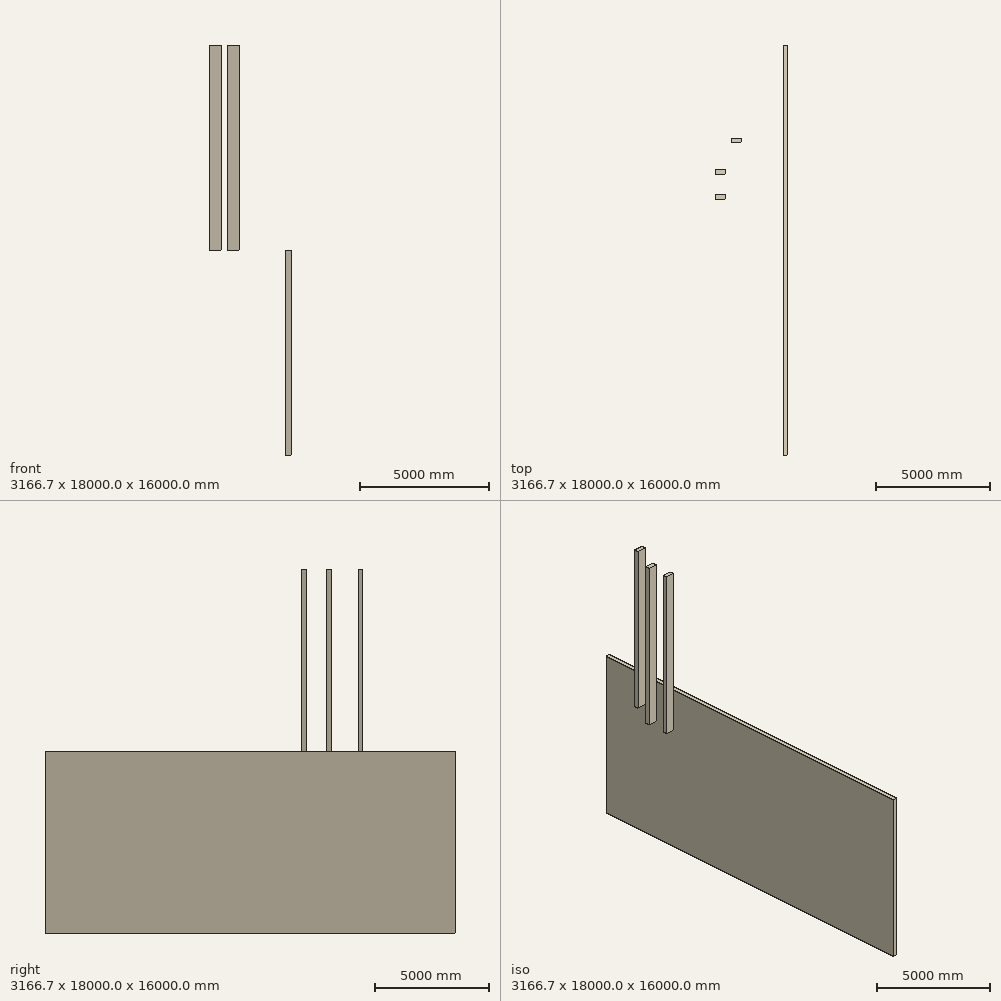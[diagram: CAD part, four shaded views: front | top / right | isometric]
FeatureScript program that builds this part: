
annotation { "Feature Type Name" : "Feature", "Feature Type Description" : "" }
export const myFeature = defineFeature(function(context is Context, id is Id, definition is map)
    precondition{}
    {
        {
            var Q0;
            Q0=qCreatedBy(makeId("Top.planeOp"),FACE);
            var sketch = newSketch(context, id + "F0", { "sketchPlane" : qUnion([Q0])});
            skLineSegment(sketch, "E0.bottom", {"start": v(48.72, -62.87) * mm, "end": v(248.72, -62.87) * mm});
            skLineSegment(sketch, "E0.top", {"start": v(48.72, 17937.13) * mm, "end": v(248.72, 17937.13) * mm});
            skLineSegment(sketch, "E0.left", {"start": v(48.72, -62.87) * mm, "end": v(48.72, 17937.13) * mm});
            skLineSegment(sketch, "E0.right", {"start": v(248.72, -62.87) * mm, "end": v(248.72, 17937.13) * mm});
            skPoint(sketch, "E0.middle", {"position": v(148.72, 8937.13) * mm});
            skSolve(sketch);
        }
        {
            var Q0;
            Q0=makeQuery(id+"F0.imprint","IMPRINT",FACE,{"disambiguationData":[TD([[makeQuery(id+"F0.imprint","IMPRINT",EDGE,{"derivedFrom":sQuery(id+"F0.wireOp",EDGE,"E0.bottom")}),1.0]])]});
            extrude(context, id + "F1", {"entities" : qUnion([Q0]), "depth" : 8000 * mm, "offsetDistance" : 25 * mm});
        }
        {
            var Q0;
            Q0=makeQuery(id+"F1.opExtrude","CAP_FACE",FACE,{"disambiguationData":[OSD([sQuery(id+"F0.wireOp",EDGE,"E0.bottom"),sQuery(id+"F0.wireOp",EDGE,"E0.top"),sQuery(id+"F0.wireOp",EDGE,"E0.left"),sQuery(id+"F0.wireOp",EDGE,"E0.right")])],"isStart":false});
            var sketch = newSketch(context, id + "F2", { "sketchPlane" : qUnion([Q0])});
            skLineSegment(sketch, "E1.bottom", {"start": v(-1766.05, 13672.67) * mm, "end": v(-2216.05, 13672.67) * mm});
            skLineSegment(sketch, "E1.top", {"start": v(-1766.05, 13872.67) * mm, "end": v(-2216.05, 13872.67) * mm});
            skLineSegment(sketch, "E1.left", {"start": v(-1766.05, 13672.67) * mm, "end": v(-1766.05, 13872.67) * mm});
            skLineSegment(sketch, "E1.right", {"start": v(-2216.05, 13672.67) * mm, "end": v(-2216.05, 13872.67) * mm});
            skPoint(sketch, "E1.middle", {"position": v(-1991.05, 13772.67) * mm});
            skLineSegment(sketch, "E2.bottom", {"start": v(-2467.97, 12275.48) * mm, "end": v(-2917.97, 12275.48) * mm});
            skLineSegment(sketch, "E2.top", {"start": v(-2467.97, 12475.48) * mm, "end": v(-2917.97, 12475.48) * mm});
            skLineSegment(sketch, "E2.left", {"start": v(-2467.97, 12275.48) * mm, "end": v(-2467.97, 12475.48) * mm});
            skLineSegment(sketch, "E2.right", {"start": v(-2917.97, 12275.48) * mm, "end": v(-2917.97, 12475.48) * mm});
            skPoint(sketch, "E2.middle", {"position": v(-2692.97, 12375.48) * mm});
            skLineSegment(sketch, "E3.bottom", {"start": v(-2467.97, 11182.5) * mm, "end": v(-2917.97, 11182.5) * mm});
            skLineSegment(sketch, "E3.top", {"start": v(-2467.97, 11382.5) * mm, "end": v(-2917.97, 11382.5) * mm});
            skLineSegment(sketch, "E3.left", {"start": v(-2467.97, 11182.5) * mm, "end": v(-2467.97, 11382.5) * mm});
            skLineSegment(sketch, "E3.right", {"start": v(-2917.97, 11182.5) * mm, "end": v(-2917.97, 11382.5) * mm});
            skPoint(sketch, "E3.middle", {"position": v(-2692.97, 11282.5) * mm});
            skSolve(sketch);
        }
        {
            var Q0;
            Q0=makeQuery(id+"F2.imprint","IMPRINT",FACE,{"disambiguationData":[TD([[makeQuery(id+"F2.imprint","IMPRINT",EDGE,{"derivedFrom":sQuery(id+"F2.wireOp",EDGE,"E1.bottom")}),-1.0]])]});
            var Q1;
            Q1=makeQuery(id+"F2.imprint","IMPRINT",FACE,{"disambiguationData":[TD([[makeQuery(id+"F2.imprint","IMPRINT",EDGE,{"derivedFrom":sQuery(id+"F2.wireOp",EDGE,"E2.bottom")}),-1.0]])]});
            var Q2;
            Q2=makeQuery(id+"F2.imprint","IMPRINT",FACE,{"disambiguationData":[TD([[makeQuery(id+"F2.imprint","IMPRINT",EDGE,{"derivedFrom":sQuery(id+"F2.wireOp",EDGE,"E3.bottom")}),-1.0]])]});
            extrude(context, id + "F3", {"entities" : qUnion([Q0, Q1, Q2]), "depth" : 8000 * mm, "offsetDistance" : 25 * mm});
        }
    });
